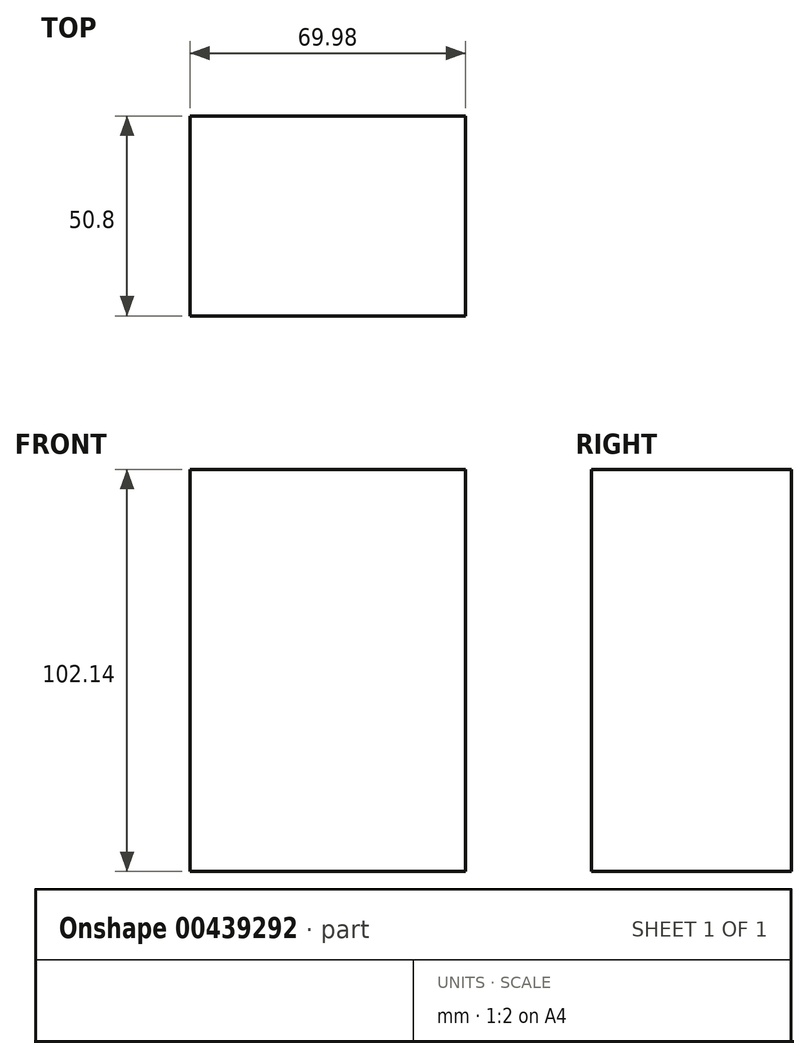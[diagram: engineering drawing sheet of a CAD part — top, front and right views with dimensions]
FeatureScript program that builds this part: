
annotation { "Feature Type Name" : "Feature", "Feature Type Description" : "" }
export const myFeature = defineFeature(function(context is Context, id is Id, definition is map)
    precondition{}
    {
        {
            var Q0;
            Q0=qCreatedBy(makeId("Front.planeOp"),FACE);
            var sketch = newSketch(context, id + "F0", { "sketchPlane" : qUnion([Q0])});
            skLineSegment(sketch, "E0.bottom", {"start": v(35, 51.07) * mm, "end": v(-35, 51.07) * mm});
            skLineSegment(sketch, "E0.top", {"start": v(35, -51.07) * mm, "end": v(-35, -51.07) * mm});
            skLineSegment(sketch, "E0.left", {"start": v(35, 51.07) * mm, "end": v(35, -51.07) * mm});
            skLineSegment(sketch, "E0.right", {"start": v(-35, 51.07) * mm, "end": v(-35, -51.07) * mm});
            skPoint(sketch, "E0.middle", {"position": v(0, 0) * mm});
            skSolve(sketch);
        }
        {
            var Q0;
            Q0 = qSketchRegion(id + "F0", true);
            extrude(context, id + "F1", {"entities" : qUnion([Q0]), "depth" : 25.4 * mm});
        }
        {
            var Q0;
            Q0=makeQuery(id+"F1.opExtrude","CAP_FACE",FACE,{"disambiguationData":[OSD([sQuery(id+"F0.wireOp",EDGE,"E0.bottom"),sQuery(id+"F0.wireOp",EDGE,"E0.top"),sQuery(id+"F0.wireOp",EDGE,"E0.left"),sQuery(id+"F0.wireOp",EDGE,"E0.right")])],"isStart":true});
            extrude(context, id + "F2", {"entities" : qUnion([Q0]), "operationType" : NewBodyOperationType.ADD, "depth" : 25.4 * mm});
        }
    });
